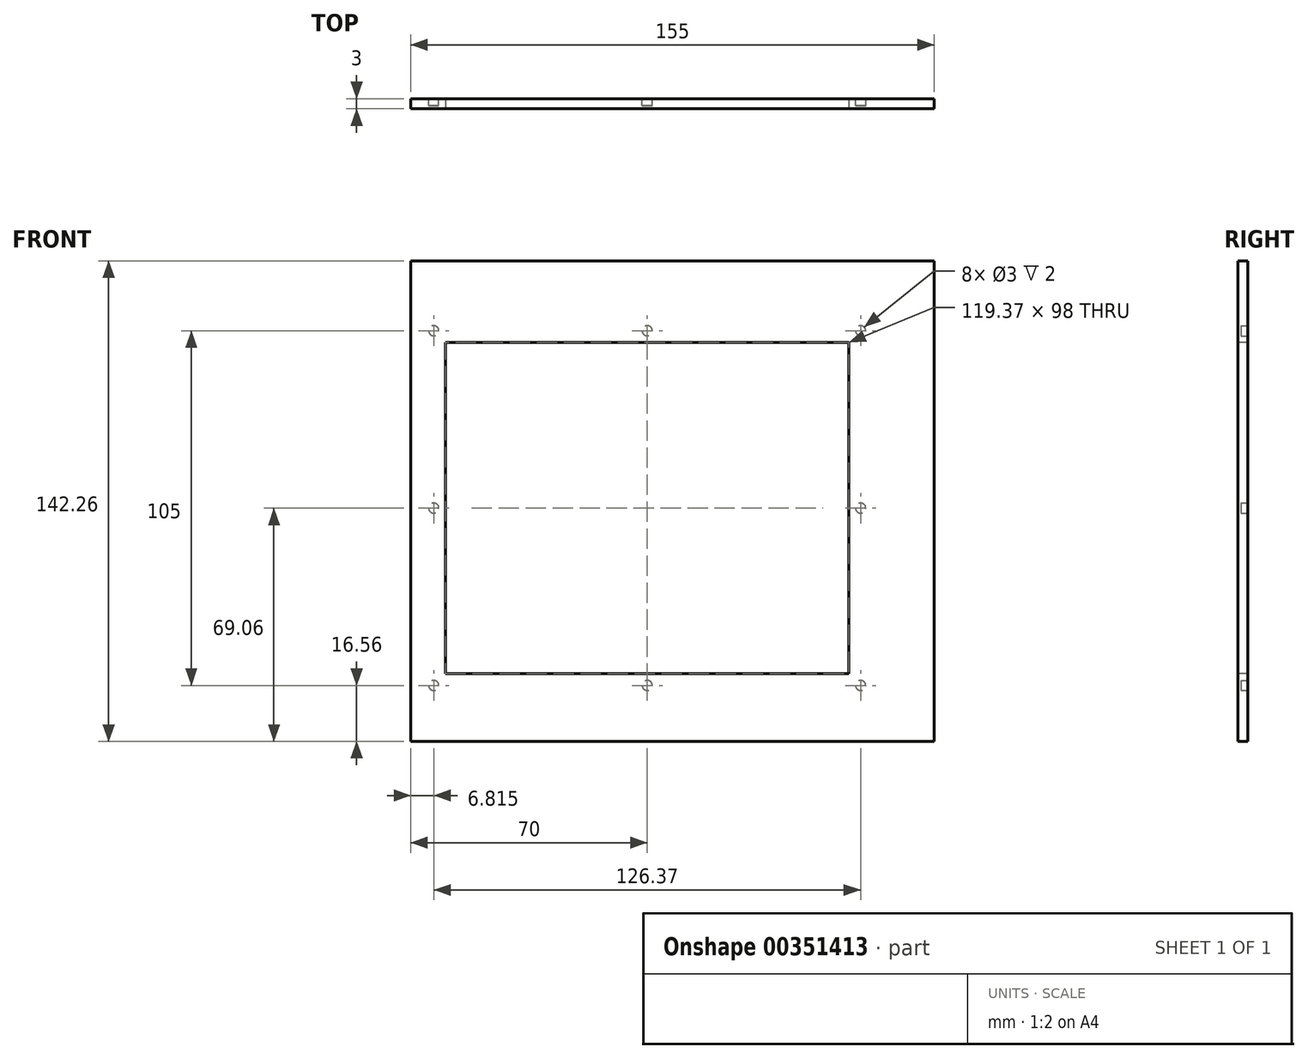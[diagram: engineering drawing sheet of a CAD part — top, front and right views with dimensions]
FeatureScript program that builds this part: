
annotation { "Feature Type Name" : "Feature", "Feature Type Description" : "" }
export const myFeature = defineFeature(function(context is Context, id is Id, definition is map)
    precondition{}
    {
        {
            var Q0;
            Q0=qCreatedBy(makeId("Front.planeOp"),FACE);
            var sketch = newSketch(context, id + "F0", { "sketchPlane" : qUnion([Q0])});
            skLineSegment(sketch, "E0.bottom", {"start": v(77.5, 65.38) * mm, "end": v(-77.5, 65.38) * mm});
            skLineSegment(sketch, "E0.top", {"start": v(77.5, -65.38) * mm, "end": v(-77.5, -65.38) * mm});
            skLineSegment(sketch, "E0.left", {"start": v(77.5, 65.38) * mm, "end": v(77.5, -65.38) * mm});
            skLineSegment(sketch, "E0.right", {"start": v(-77.5, 65.38) * mm, "end": v(-77.5, -65.38) * mm});
            skPoint(sketch, "E0.middle", {"position": v(0, 0) * mm});
            skSolve(sketch);
        }
        {
            var Q0;
            Q0=qSketchRegion(id+"F0",true);
            extrude(context, id + "F1", {"entities" : qUnion([Q0]), "depth" : 3 * mm});
        }
        {
            var Q0;
            Q0=makeQuery(id+"F1.opExtrude","CAP_FACE",FACE,{"disambiguationData":[OSD([sQuery(id+"F0.wireOp",EDGE,"E0.bottom"),sQuery(id+"F0.wireOp",EDGE,"E0.top"),sQuery(id+"F0.wireOp",EDGE,"E0.left"),sQuery(id+"F0.wireOp",EDGE,"E0.right")])],"isStart":true});
            var sketch = newSketch(context, id + "F2", { "sketchPlane" : qUnion([Q0])});
            skLineSegment(sketch, "E1.bottom", {"start": v(64.19, 49.68) * mm, "end": v(-49.19, 49.68) * mm});
            skLineSegment(sketch, "E1.top", {"start": v(64.19, -42.32) * mm, "end": v(-49.19, -42.32) * mm});
            skLineSegment(sketch, "E1.left", {"start": v(64.19, 49.68) * mm, "end": v(64.18, -42.32) * mm});
            skLineSegment(sketch, "E1.right", {"start": v(-49.19, 49.68) * mm, "end": v(-49.19, -42.32) * mm});
            skLineSegment(sketch, "E2", {"start": v(64.19, 49.68) * mm, "end": v(-49.19, -42.32) * mm, "construction": true});
            skLineSegment(sketch, "E3", {"start": v(-49.19, 49.68) * mm, "end": v(64.19, -42.32) * mm, "construction": true});
            skLineSegment(sketch, "E4.bottom", {"start": v(64.19, 49.68) * mm, "end": v(7.5, 49.68) * mm, "construction": true});
            skLineSegment(sketch, "E4.top", {"start": v(64.19, -42.32) * mm, "end": v(7.5, -42.32) * mm, "construction": true});
            skLineSegment(sketch, "E4.left", {"start": v(64.18, 49.68) * mm, "end": v(64.18, -42.32) * mm, "construction": true});
            skLineSegment(sketch, "E4.right", {"start": v(7.5, 49.68) * mm, "end": v(7.5, -42.32) * mm, "construction": true});
            skSolve(sketch);
        }
        {
            var Q0;
            Q0=qSketchRegion(id+"F2",true);
            extrude(context, id + "F3", {"entities" : qUnion([Q0]), "operationType" : NewBodyOperationType.REMOVE, "oppositeDirection" : true, "depth" : 25 * mm});
        }
        {
            var Q0;
            Q0=makeQuery(id+"F1.opExtrude","CAP_FACE",FACE,{"disambiguationData":[OSD([sQuery(id+"F0.wireOp",EDGE,"E0.bottom"),sQuery(id+"F0.wireOp",EDGE,"E0.top"),sQuery(id+"F0.wireOp",EDGE,"E0.left"),sQuery(id+"F0.wireOp",EDGE,"E0.right")])],"isStart":false});
            var sketch = newSketch(context, id + "F4", { "sketchPlane" : qUnion([Q0])});
            skLineSegment(sketch, "E5.bottom", {"start": v(-67.19, 52.68) * mm, "end": v(52.19, 52.68) * mm});
            skLineSegment(sketch, "E5.top", {"start": v(-67.18, -45.32) * mm, "end": v(52.19, -45.32) * mm});
            skLineSegment(sketch, "E5.left", {"start": v(-67.19, 52.68) * mm, "end": v(-67.18, -45.32) * mm});
            skLineSegment(sketch, "E5.right", {"start": v(52.19, 52.68) * mm, "end": v(52.19, -45.32) * mm});
            skSolve(sketch);
        }
        {
            var Q0;
            Q0=qSketchRegion(id+"F4",true);
            extrude(context, id + "F5", {"entities" : qUnion([Q0]), "operationType" : NewBodyOperationType.REMOVE, "oppositeDirection" : true, "depth" : 25 * mm});
        }
        {
            var Q0;
            Q0=makeQuery(id+"F1.opExtrude","CAP_FACE",FACE,{"disambiguationData":[OSD([sQuery(id+"F0.wireOp",EDGE,"E0.bottom"),sQuery(id+"F0.wireOp",EDGE,"E0.top"),sQuery(id+"F0.wireOp",EDGE,"E0.left"),sQuery(id+"F0.wireOp",EDGE,"E0.right")])],"isStart":true});
            var sketch = newSketch(context, id + "F6", { "sketchPlane" : qUnion([Q0])});
            skLineSegment(sketch, "E6.bottom", {"start": v(-55.69, 56.18) * mm, "end": v(70.69, 56.18) * mm, "construction": true});
            skLineSegment(sketch, "E6.top", {"start": v(-55.69, -48.82) * mm, "end": v(70.69, -48.82) * mm, "construction": true});
            skLineSegment(sketch, "E6.left", {"start": v(-55.69, 56.18) * mm, "end": v(-55.69, -48.82) * mm, "construction": true});
            skLineSegment(sketch, "E6.right", {"start": v(70.69, 56.18) * mm, "end": v(70.69, -48.82) * mm, "construction": true});
            skCircle(sketch, "E7", {"center": v(-55.69, 56.18) * mm, "radius": 1.5 * mm});
            skCircle(sketch, "E8", {"center": v(70.69, 56.18) * mm, "radius": 1.5 * mm});
            skCircle(sketch, "E9", {"center": v(70.69, -48.82) * mm, "radius": 1.5 * mm});
            skCircle(sketch, "E10", {"center": v(-55.69, -48.82) * mm, "radius": 1.5 * mm});
            skCircle(sketch, "E11", {"center": v(7.5, -48.82) * mm, "radius": 1.5 * mm});
            skCircle(sketch, "E12", {"center": v(-55.69, 3.68) * mm, "radius": 1.5 * mm});
            skCircle(sketch, "E13", {"center": v(70.69, 3.68) * mm, "radius": 1.5 * mm});
            skCircle(sketch, "E14", {"center": v(7.5, 56.18) * mm, "radius": 1.5 * mm});
            skSolve(sketch);
        }
        {
            var Q0;
            Q0=qSketchRegion(id+"F6",true);
            extrude(context, id + "F7", {"entities" : qUnion([Q0]), "operationType" : NewBodyOperationType.REMOVE, "oppositeDirection" : true, "depth" : 2 * mm});
        }
        {
            var Q0;
            Q0=makeQuery(id+"F1.opExtrude","SWEPT_FACE",FACE,{"disambiguationData":[OSD([sQuery(id+"F0.wireOp",EDGE,"E0.bottom")])]});
            var sketch = newSketch(context, id + "F8", { "sketchPlane" : qUnion([Q0])});
            skLineSegment(sketch, "E15.bottom", {"start": v(-77.5, 0) * mm, "end": v(77.5, 0) * mm});
            skLineSegment(sketch, "E15.top", {"start": v(-77.5, -3) * mm, "end": v(77.5, -3) * mm});
            skLineSegment(sketch, "E15.left", {"start": v(-77.5, 0) * mm, "end": v(-77.5, -3) * mm});
            skLineSegment(sketch, "E15.right", {"start": v(77.5, 0) * mm, "end": v(77.5, -3) * mm});
            skSolve(sketch);
        }
        {
            var Q0;
            Q0=qSketchRegion(id+"F8",true);
            extrude(context, id + "F9", {"entities" : qUnion([Q0]), "operationType" : NewBodyOperationType.ADD, "depth" : 11.5 * mm});
        }
    });
